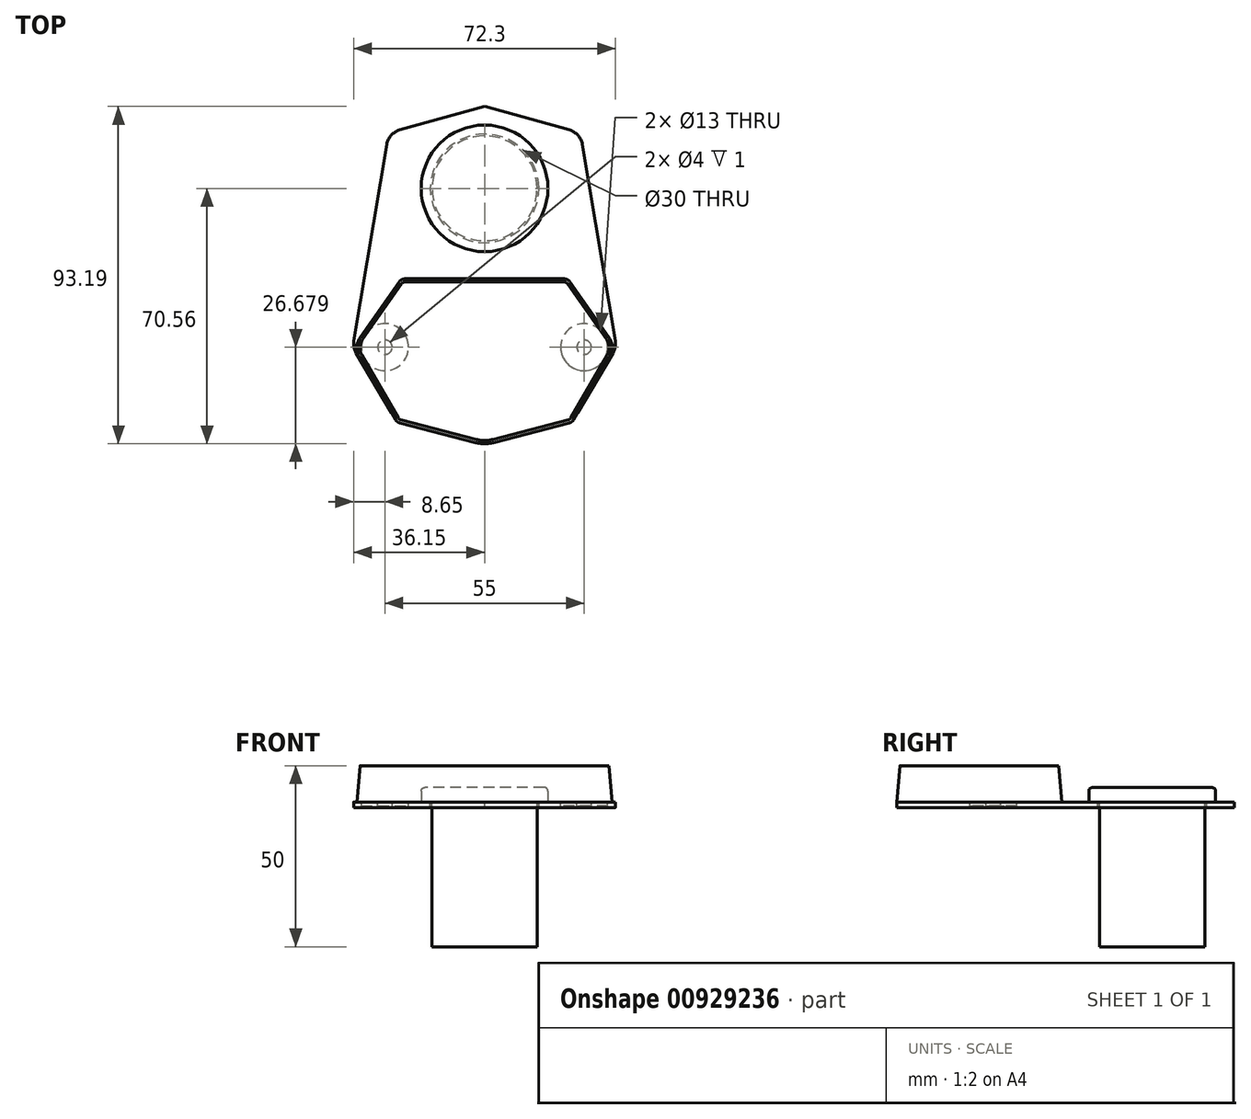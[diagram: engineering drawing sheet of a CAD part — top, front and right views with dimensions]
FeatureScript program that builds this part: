
annotation { "Feature Type Name" : "Feature", "Feature Type Description" : "" }
export const myFeature = defineFeature(function(context is Context, id is Id, definition is map)
    precondition{}
    {
        {
            var Q0;
            Q0=qCreatedBy(makeId("Top.planeOp"),FACE);
            var sketch = newSketch(context, id + "F0", { "sketchPlane" : qUnion([Q0])});
            skLineSegment(sketch, "E0", {"start": v(0, 0) * mm, "end": v(21.97, 0) * mm});
            skLineSegment(sketch, "E1", {"start": v(23.6, -0.85) * mm, "end": v(34.38, -16.23) * mm});
            skLineSegment(sketch, "E2", {"start": v(34.61, -21.6) * mm, "end": v(24.62, -38.9) * mm});
            skLineSegment(sketch, "E3", {"start": v(23.4, -39.84) * mm, "end": v(2.5, -45.24) * mm});
            skLineSegment(sketch, "E4.MirrorCS", {"start": v(0, 0) * mm, "end": v(-21.97, 0) * mm});
            skLineSegment(sketch, "E5.MirrorCS", {"start": v(-23.6, -0.85) * mm, "end": v(-34.38, -16.23) * mm});
            skLineSegment(sketch, "E6.MirrorCS", {"start": v(-34.61, -21.6) * mm, "end": v(-24.62, -38.9) * mm});
            skLineSegment(sketch, "E7.MirrorCS", {"start": v(-23.4, -39.84) * mm, "end": v(-2.5, -45.24) * mm});
            skPoint(sketch, "E8.visualSharp", {"position": v(-23.01, 0) * mm});
            skArc(sketch, "E8.filletArc", {"start": v(-21.97, 0) * mm, "mid": v(-22.9, -0.23) * mm, "end": v(-23.6, -0.85) * mm});
            skPoint(sketch, "E9.visualSharp", {"position": v(23.01, 0) * mm});
            skArc(sketch, "E9.filletArc", {"start": v(23.6, -0.85) * mm, "mid": v(22.9, -0.23) * mm, "end": v(21.97, 0) * mm});
            skPoint(sketch, "E10.visualSharp", {"position": v(-24.2, -39.63) * mm});
            skArc(sketch, "E10.filletArc", {"start": v(-24.62, -38.9) * mm, "mid": v(-24.1, -39.5) * mm, "end": v(-23.4, -39.84) * mm});
            skPoint(sketch, "E11.visualSharp", {"position": v(24.2, -39.63) * mm});
            skArc(sketch, "E11.filletArc", {"start": v(23.4, -39.84) * mm, "mid": v(24.1, -39.5) * mm, "end": v(24.62, -38.9) * mm});
            skPoint(sketch, "E12.visualSharp", {"position": v(-36.2, -18.84) * mm});
            skArc(sketch, "E12.filletArc", {"start": v(-34.38, -16.23) * mm, "mid": v(-35.28, -18.88) * mm, "end": v(-34.61, -21.6) * mm});
            skPoint(sketch, "E13.visualSharp", {"position": v(36.2, -18.84) * mm});
            skArc(sketch, "E13.filletArc", {"start": v(34.61, -21.6) * mm, "mid": v(35.28, -18.88) * mm, "end": v(34.38, -16.23) * mm});
            skPoint(sketch, "E14.visualSharp", {"position": v(0, -45.88) * mm});
            skArc(sketch, "E14.filletArc", {"start": v(-2.5, -45.24) * mm, "mid": v(0, -45.56) * mm, "end": v(2.5, -45.24) * mm});
            skSolve(sketch);
        }
        {
            var Q0;
            Q0=makeQuery(id+"F0.imprint","IMPRINT",FACE,{"disambiguationData":[TD([[makeQuery(id+"F0.imprint","IMPRINT",EDGE,{"derivedFrom":sQuery(id+"F0.wireOp",EDGE,"E0")}),-1.0]])]});
            extrude(context, id + "F1", {"entities" : qUnion([Q0]), "depth" : 10 * mm, "offsetDistance" : 25 * mm, "hasDraft" : true, "draftAngle" : 5 * degree, "draftPullDirection" : true});
        }
        {
            var Q0;
            Q0=makeQuery(id+"F1.opExtrude","CAP_FACE",FACE,{"disambiguationData":[OSD([sQuery(id+"F0.wireOp",EDGE,"E0"),sQuery(id+"F0.wireOp",EDGE,"E1"),sQuery(id+"F0.wireOp",EDGE,"E2"),sQuery(id+"F0.wireOp",EDGE,"E3"),sQuery(id+"F0.wireOp",EDGE,"E4.MirrorCS"),sQuery(id+"F0.wireOp",EDGE,"E5.MirrorCS"),sQuery(id+"F0.wireOp",EDGE,"E6.MirrorCS"),sQuery(id+"F0.wireOp",EDGE,"E7.MirrorCS"),sQuery(id+"F0.wireOp",EDGE,"E8.filletArc"),sQuery(id+"F0.wireOp",EDGE,"E9.filletArc"),sQuery(id+"F0.wireOp",EDGE,"E10.filletArc"),sQuery(id+"F0.wireOp",EDGE,"E11.filletArc"),sQuery(id+"F0.wireOp",EDGE,"E12.filletArc"),sQuery(id+"F0.wireOp",EDGE,"E13.filletArc"),sQuery(id+"F0.wireOp",EDGE,"E14.filletArc")])],"isStart":true});
            var sketch = newSketch(context, id + "F2", { "sketchPlane" : qUnion([Q0])});
            skCircle(sketch, "E15", {"center": v(-27.5, 18.88) * mm, "radius": 2 * mm});
            skCircle(sketch, "E16", {"center": v(27.5, 18.88) * mm, "radius": 2 * mm});
            skCircle(sketch, "E17", {"center": v(-27.5, 18.88) * mm, "radius": 6.5 * mm});
            skCircle(sketch, "E18", {"center": v(27.5, 18.88) * mm, "radius": 6.5 * mm});
            skSolve(sketch);
        }
        {
            var Q0;
            Q0=makeQuery(id+"F2.imprint","IMPRINT",FACE,{"disambiguationData":[TD([[makeQuery(id+"F2.imprint","IMPRINT",EDGE,{"derivedFrom":sQuery(id+"F2.wireOp",EDGE,"E15")}),-1.0]])]});
            var Q1;
            Q1=makeQuery(id+"F2.imprint","IMPRINT",FACE,{"disambiguationData":[TD([[makeQuery(id+"F2.imprint","IMPRINT",EDGE,{"derivedFrom":sQuery(id+"F2.wireOp",EDGE,"E16")}),-1.0]])]});
            extrude(context, id + "F3", {"entities" : qUnion([Q0, Q1]), "operationType" : NewBodyOperationType.ADD, "depth" : 1 * mm, "offsetDistance" : 25 * mm});
        }
        {
            var Q0;
            Q0=qCreatedBy(makeId("Top.planeOp"),FACE);
            var sketch = newSketch(context, id + "F4", { "sketchPlane" : qUnion([Q0])});
            skCircle(sketch, "E19", {"center": v(0, 25) * mm, "radius": 17.5 * mm});
            skSolve(sketch);
        }
        {
            var Q0;
            Q0=makeQuery(id+"F4.imprint","IMPRINT",FACE,{"disambiguationData":[TD([[makeQuery(id+"F4.imprint","IMPRINT",EDGE,{"derivedFrom":sQuery(id+"F4.wireOp",EDGE,"E19")}),1.0]])]});
            extrude(context, id + "F5", {"entities" : qUnion([Q0]), "depth" : 4 * mm, "offsetDistance" : 25 * mm});
        }
        {
            var Q0;
            Q0=makeQuery(id+"F5.opExtrude","CAP_EDGE",EDGE,{"disambiguationData":[OSD([sQuery(id+"F4.wireOp",EDGE,"E19")])],"isStart":false});
            fillet(context, id + "F6", {"entities" : qUnion([Q0]), "tangentPropagation" : true, "radius" : 1 * mm, "defaultsChanged" : true, "vertexSettings" : [], "allowEdgeOverflow" : false});
        }
        {
            var Q0;
            Q0=makeQuery(id+"F5.opExtrude","CAP_FACE",FACE,{"disambiguationData":[OSD([sQuery(id+"F4.wireOp",EDGE,"E19")])],"isStart":true});
            var sketch = newSketch(context, id + "F7", { "sketchPlane" : qUnion([Q0])});
            skCircle(sketch, "E20", {"center": v(0, -25) * mm, "radius": 14.5 * mm});
            skSolve(sketch);
        }
        {
            var Q0;
            Q0=makeQuery(id+"F7.imprint","IMPRINT",FACE,{"disambiguationData":[TD([[makeQuery(id+"F7.imprint","IMPRINT",EDGE,{"derivedFrom":sQuery(id+"F7.wireOp",EDGE,"E20")}),1.0]])]});
            extrude(context, id + "F8", {"entities" : qUnion([Q0]), "operationType" : NewBodyOperationType.ADD, "depth" : 40 * mm, "offsetDistance" : 25 * mm});
        }
        {
            var Q0;
            Q0=qCreatedBy(makeId("Top.planeOp"),FACE);
            var sketch = newSketch(context, id + "F9", { "sketchPlane" : qUnion([Q0])});
            skLineSegment(sketch, "E21.MirrorCS", {"start": v(-35.46, -20.46) * mm, "end": v(-24.62, -38.86) * mm});
            skLineSegment(sketch, "E22.MirrorCS", {"start": v(-23.4, -39.78) * mm, "end": v(-2.5, -45.19) * mm});
            skPoint(sketch, "E23.visualSharp", {"position": v(-24.2, -39.57) * mm});
            skArc(sketch, "E23.filletArc", {"start": v(-24.62, -38.86) * mm, "mid": v(-24.1, -39.44) * mm, "end": v(-23.4, -39.78) * mm});
            skPoint(sketch, "E24.visualSharp", {"position": v(-36.38, -18.9) * mm});
            skLineSegment(sketch, "E25", {"start": v(-36.08, -17.1) * mm, "end": v(-27, 37.14) * mm});
            skLineSegment(sketch, "E26", {"start": v(-23.41, 41.13) * mm, "end": v(0, 47.63) * mm});
            skArc(sketch, "E27.filletArc", {"start": v(-36.08, -17.1) * mm, "mid": v(-36.07, -18.84) * mm, "end": v(-35.46, -20.46) * mm});
            skPoint(sketch, "E28.visualSharp", {"position": v(-26.48, 40.28) * mm});
            skArc(sketch, "E28.filletArc", {"start": v(-23.41, 41.13) * mm, "mid": v(-25.8, 39.66) * mm, "end": v(-27, 37.14) * mm});
            skLineSegment(sketch, "E29.MirrorCS", {"start": v(23.41, 41.13) * mm, "end": v(0, 47.63) * mm});
            skArc(sketch, "E30.MirrorCS", {"start": v(24.62, -38.86) * mm, "mid": v(24.1, -39.44) * mm, "end": v(23.4, -39.78) * mm});
            skArc(sketch, "E31.MirrorCS", {"start": v(36.08, -17.1) * mm, "mid": v(36.07, -18.84) * mm, "end": v(35.46, -20.46) * mm});
            skArc(sketch, "E32.MirrorCS", {"start": v(23.41, 41.13) * mm, "mid": v(25.8, 39.66) * mm, "end": v(27, 37.14) * mm});
            skPoint(sketch, "E33.MirrorP", {"position": v(36.38, -18.9) * mm});
            skPoint(sketch, "E34.MirrorP", {"position": v(24.2, -39.57) * mm});
            skLineSegment(sketch, "E35.MirrorCS", {"start": v(35.46, -20.46) * mm, "end": v(24.62, -38.86) * mm});
            skPoint(sketch, "E36.MirrorP", {"position": v(26.48, 40.28) * mm});
            skLineSegment(sketch, "E37.MirrorCS", {"start": v(23.4, -39.78) * mm, "end": v(2.5, -45.19) * mm});
            skLineSegment(sketch, "E38.MirrorCS", {"start": v(36.08, -17.1) * mm, "end": v(27, 37.14) * mm});
            skPoint(sketch, "E39.visualSharp", {"position": v(0, -45.83) * mm});
            skArc(sketch, "E39.filletArc", {"start": v(-2.5, -45.19) * mm, "mid": v(0, -45.5) * mm, "end": v(2.5, -45.19) * mm});
            skCircle(sketch, "E40", {"center": v(27.5, -18.88) * mm, "radius": 6.5 * mm});
            skCircle(sketch, "E41", {"center": v(-27.5, -18.88) * mm, "radius": 6.5 * mm});
            skCircle(sketch, "E42", {"center": v(0, 25) * mm, "radius": 15 * mm});
            skSolve(sketch);
        }
        {
            var Q0;
            Q0=makeQuery(id+"F9.imprint","IMPRINT",FACE,{"disambiguationData":[TD([[makeQuery(id+"F9.imprint","IMPRINT",EDGE,{"derivedFrom":sQuery(id+"F9.wireOp",EDGE,"E21.MirrorCS")}),1.0]])]});
            extrude(context, id + "F10", {"entities" : qUnion([Q0]), "oppositeDirection" : true, "depth" : 1.52 * mm, "offsetDistance" : 25 * mm});
        }
    });
